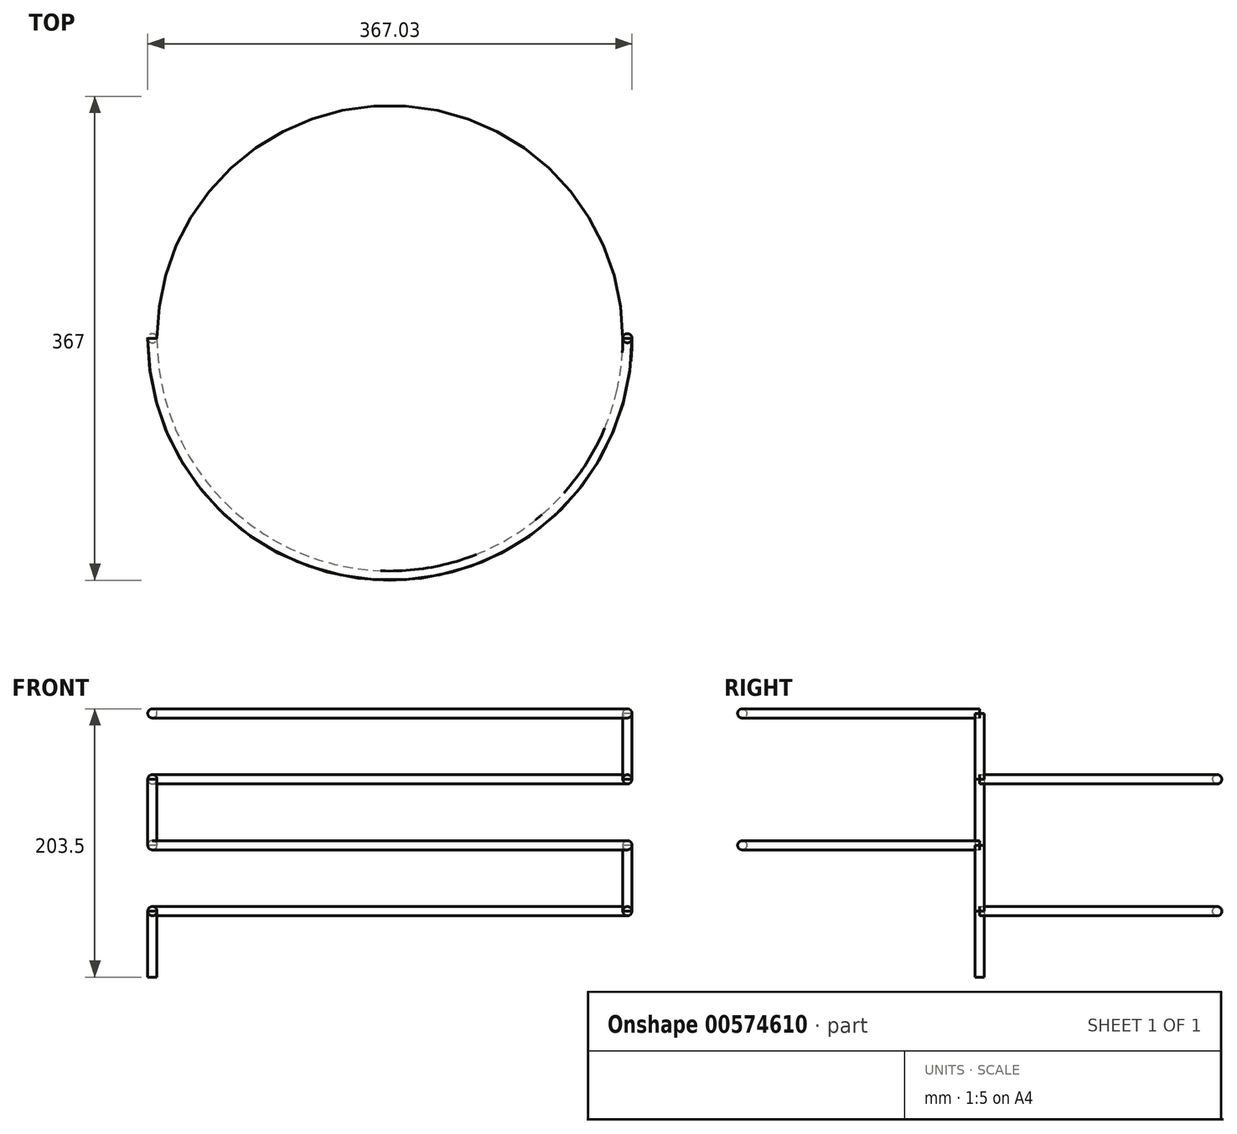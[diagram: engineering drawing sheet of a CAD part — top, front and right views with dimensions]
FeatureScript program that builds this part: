
annotation { "Feature Type Name" : "Feature", "Feature Type Description" : "" }
export const myFeature = defineFeature(function(context is Context, id is Id, definition is map)
    precondition{}
    {
        {
            var Q0;
            Q0=qCreatedBy(makeId("Front.planeOp"),FACE);
            var sketch = newSketch(context, id + "F0", { "sketchPlane" : qUnion([Q0])});
            skCircle(sketch, "E0", {"center": v(-180, 0) * mm, "radius": 3.5 * mm});
            skLineSegment(sketch, "E1", {"start": v(0, 14.5) * mm, "end": v(0, -10.87) * mm});
            skCircle(sketch, "E2", {"center": v(180, 50) * mm, "radius": 3.5 * mm});
            skCircle(sketch, "E3", {"center": v(-180, -50) * mm, "radius": 3.5 * mm});
            skCircle(sketch, "E4", {"center": v(-180, -100) * mm, "radius": 3.5 * mm});
            skSolve(sketch);
        }
        {
            var Q0;
            Q0=sQuery(id+"F0.wireOp",EDGE,"E0");
            var Q1;
            Q1=sQuery(id+"F0.wireOp",EDGE,"E1");
            revolve(context, id + "F1", {"bodyType" : ToolBodyType.SURFACE, "surfaceEntities" : qUnion([Q0]), "axis" : qUnion([Q1]), "revolveType" : RevolveType.ONE_DIRECTION, "angle" : 180 * degree});
        }
        {
            var Q0;
            Q0=qCreatedBy(makeId("Top.planeOp"),FACE);
            var sketch = newSketch(context, id + "F2", { "sketchPlane" : qUnion([Q0])});
            skCircle(sketch, "E5", {"center": v(180, 0) * mm, "radius": 3.5 * mm});
            skCircle(sketch, "E6", {"center": v(-180, 0) * mm, "radius": 3.5 * mm});
            skSolve(sketch);
        }
        {
            var Q0;
            Q0=sQuery(id+"F2.wireOp",EDGE,"E5");
            extrude(context, id + "F3", {"bodyType" : ToolBodyType.SURFACE, "surfaceEntities" : qUnion([Q0]), "depth" : 50 * mm, "offsetDistance" : 25 * mm});
        }
        {
            var Q0;
            Q0=sQuery(id+"F0.wireOp",EDGE,"E2");
            var Q1;
            Q1=sQuery(id+"F0.wireOp",EDGE,"E1");
            revolve(context, id + "F4", {"bodyType" : ToolBodyType.SURFACE, "surfaceEntities" : qUnion([Q0]), "axis" : qUnion([Q1]), "revolveType" : RevolveType.ONE_DIRECTION, "angle" : 180 * degree});
        }
        {
            var Q0;
            Q0=qCreatedBy(makeId("Top.planeOp"),FACE);
            var sketch = newSketch(context, id + "F5", { "sketchPlane" : qUnion([Q0])});
            skCircle(sketch, "E7", {"center": v(-180.03, 0) * mm, "radius": 3.5 * mm});
            skSolve(sketch);
        }
        {
            var Q0;
            Q0=sQuery(id+"F5.wireOp",EDGE,"E7");
            extrude(context, id + "F6", {"bodyType" : ToolBodyType.SURFACE, "surfaceEntities" : qUnion([Q0]), "oppositeDirection" : true, "depth" : 50 * mm, "offsetDistance" : 25 * mm});
        }
        {
            var Q0;
            Q0=sQuery(id+"F0.wireOp",EDGE,"E3");
            var Q1;
            Q1=sQuery(id+"F0.wireOp",EDGE,"E1");
            revolve(context, id + "F7", {"bodyType" : ToolBodyType.SURFACE, "surfaceEntities" : qUnion([Q0]), "axis" : qUnion([Q1]), "revolveType" : RevolveType.ONE_DIRECTION, "oppositeDirection" : true, "angle" : 180 * degree});
        }
        {
            var Q0;
            Q0=sQuery(id+"F2.wireOp",EDGE,"E5");
            extrude(context, id + "F8", {"bodyType" : ToolBodyType.SURFACE, "surfaceEntities" : qUnion([Q0]), "oppositeDirection" : true, "depth" : 100 * mm, "offsetDistance" : 25 * mm, "hasSecondDirection" : true, "secondDirectionOppositeDirection" : true, "secondDirectionDepth" : 50 * mm});
        }
        {
            var Q0;
            Q0=sQuery(id+"F0.wireOp",EDGE,"E4");
            var Q1;
            Q1=sQuery(id+"F0.wireOp",EDGE,"E1");
            revolve(context, id + "F9", {"bodyType" : ToolBodyType.SURFACE, "surfaceEntities" : qUnion([Q0]), "axis" : qUnion([Q1]), "revolveType" : RevolveType.ONE_DIRECTION, "angle" : 180 * degree});
        }
        {
            var Q0;
            Q0=sQuery(id+"F2.wireOp",EDGE,"E6");
            extrude(context, id + "F10", {"bodyType" : ToolBodyType.SURFACE, "surfaceEntities" : qUnion([Q0]), "oppositeDirection" : true, "depth" : 150 * mm, "offsetDistance" : 25 * mm, "hasSecondDirection" : true, "secondDirectionOppositeDirection" : true, "secondDirectionDepth" : 100 * mm});
        }
    });
